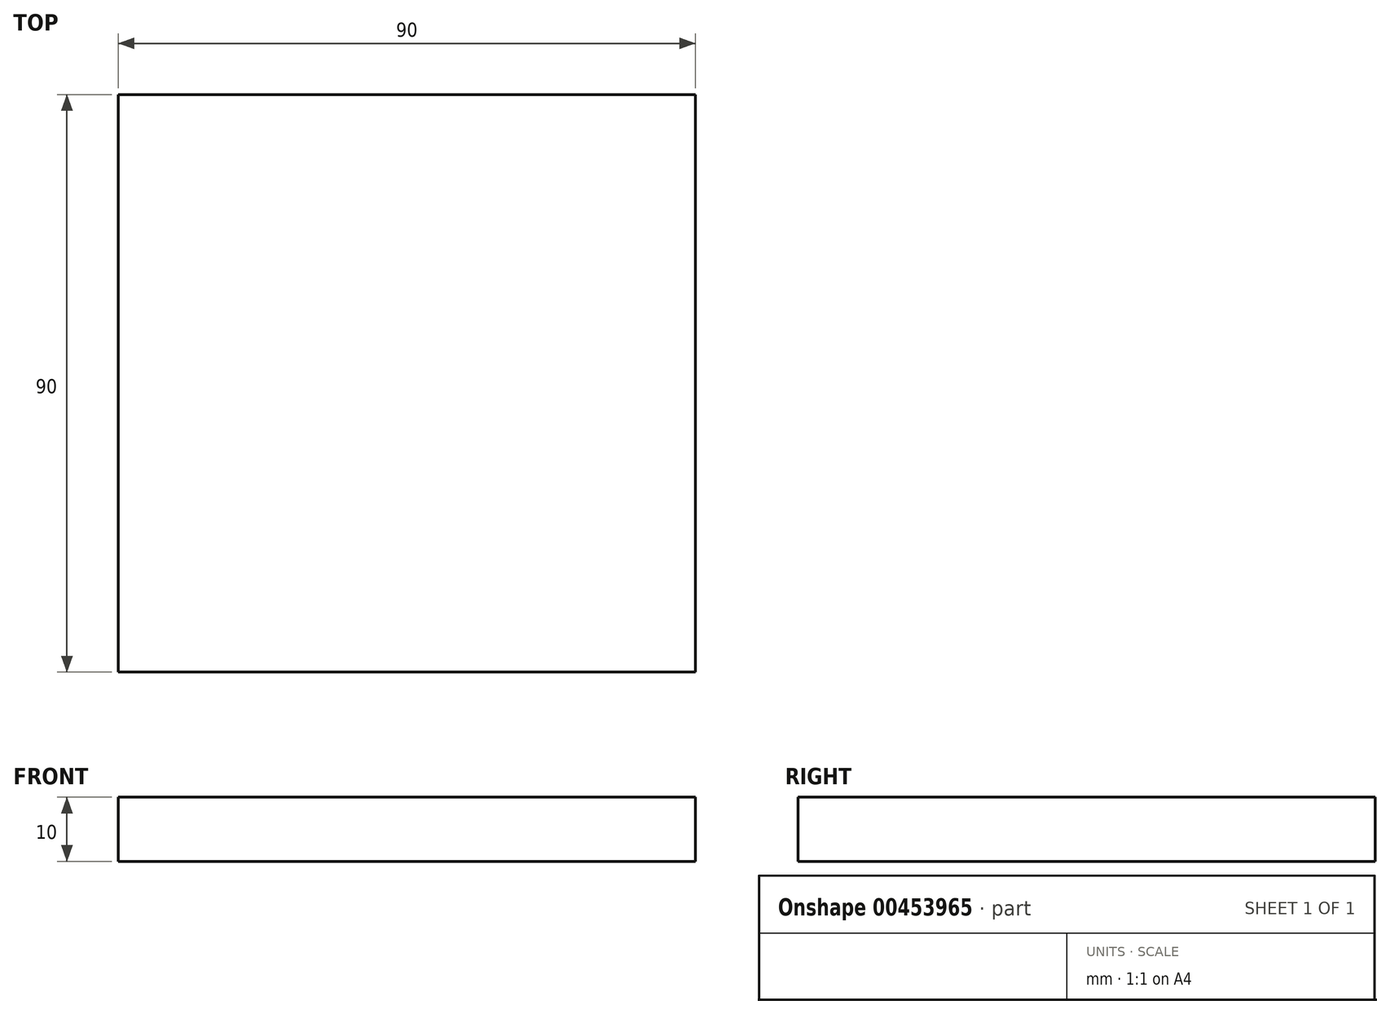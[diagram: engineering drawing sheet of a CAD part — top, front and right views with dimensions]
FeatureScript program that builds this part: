
annotation { "Feature Type Name" : "Feature", "Feature Type Description" : "" }
export const myFeature = defineFeature(function(context is Context, id is Id, definition is map)
    precondition{}
    {
        {
            var Q0;
            Q0=qCreatedBy(makeId("Top.planeOp"),FACE);
            var sketch = newSketch(context, id + "F0", { "sketchPlane" : qUnion([Q0])});
            skLineSegment(sketch, "E0.bottom", {"start": v(-51.01, 0) * mm, "end": v(38.99, 0) * mm});
            skLineSegment(sketch, "E0.top", {"start": v(-51.01, 90) * mm, "end": v(38.99, 90) * mm});
            skLineSegment(sketch, "E0.left", {"start": v(-51.01, 0) * mm, "end": v(-51.01, 90) * mm});
            skLineSegment(sketch, "E0.right", {"start": v(38.99, 0) * mm, "end": v(38.99, 90) * mm});
            skSolve(sketch);
        }
        {
            var Q0;
            Q0 = qSketchRegion(id + "F0", true);
            extrude(context, id + "F1", {"entities" : qUnion([Q0]), "depth" : 10 * mm});
        }
    });
